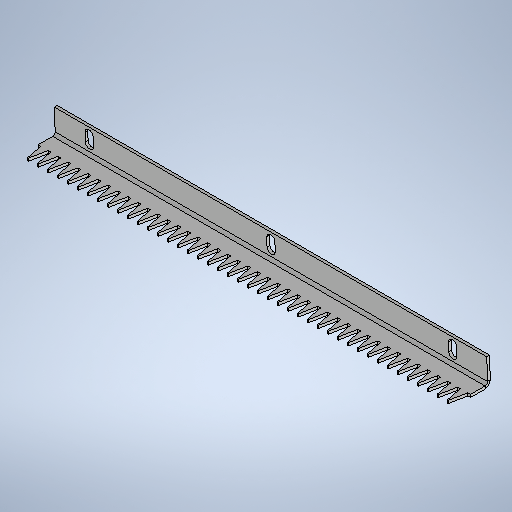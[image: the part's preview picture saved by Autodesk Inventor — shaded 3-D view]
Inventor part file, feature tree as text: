
AUTODESK INVENTOR PART (.ipt)
format: ipt  version: 2025.1 (Build 291241020, 241B)  size: 582,144 bytes
history: native  units: mm
features: other x5, sheet_metal_op x4, sketch x4, pattern_linear x2, projected_geometry x1
ambient origin geometry x8: Origin, YZ Plane, XZ Plane, XY Plane, X Axis, Y Axis, Z Axis, Center Point
bodies: Solid1 (feature_tree)
feature tree (16):
  sheet_metal_op  "Face1"
  pattern_linear  "Rectangular Pattern1"  Count1=4  [1 undecoded]
  sheet_metal_op  "Flange3"
  pattern_linear  "Rectangular Pattern2"  Spacing1=3.0mm  [1 undecoded]
  sketch  "Sketch1"  dims[d0=476.0mm d1=40.0mm]
  other  "Plate1"
  sketch  "Sketch6"  dims[d2=3.0mm]
  projected_geometry  "Projected Loop1"
  sketch  "Sketch7"  dims[d33=18.0mm]
  other  "Plate4"
  sheet_metal_op  "Bend3"
  sheet_metal_op  "Corner3"
  sketch  "Sketch8"  dims[d35=3.0mm d36=3.0mm d37=0.0mm d38=440.0mm d40=11.0mm d41=3.0mm d42=1.5mm d43=6.0mm d44=2.75mm d45=30.0mm d46=16.057029mm d47=2.75mm d48=12.0mm d49=3.0mm d50=2.75mm d51=9.0mm d53=10.0mm d54=3.0mm d55=0.0mm d56=30.0mm d58=200.0mm d79=7.0mm d80=10.0mm d81=0.5mm]
  other  "Cut1"
  other  "Cut2"
  other  "Definition1"
note: 2 required parameter values undecoded (feature->parameter linkage not recoverable at this tier; creation-order binding heuristic only, values carry confidence <= 0.55)
